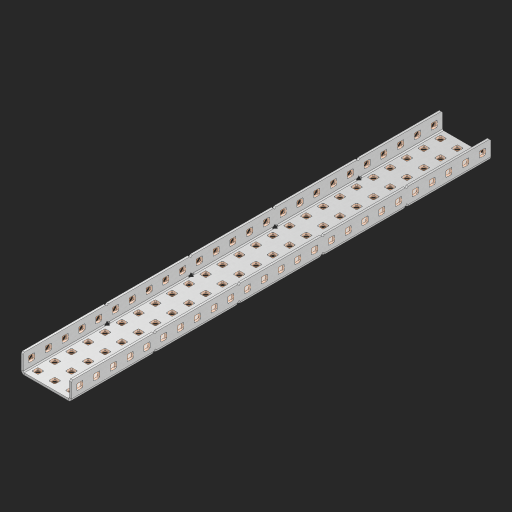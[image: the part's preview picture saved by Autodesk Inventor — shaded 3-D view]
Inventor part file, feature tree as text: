
AUTODESK INVENTOR PART (.ipt)
format: ipt  version: 2023 (Build 270158000, 158)  size: 1,567,232 bytes
history: native  units: in
note: dims shown in document units (in); Inventor stores cm internally (conversion verified against a paired STEP export)
features: other x130, extrude x124, sheet_metal_op x10, sketch x8, mirror x1, pattern_linear x1, chamfer x1
ambient origin geometry x8: Origin, YZ Plane, XZ Plane, XY Plane, X Axis, Y Axis, Z Axis, Center Point
bodies: Solid1 (feature_tree), Body (feature_tree)
feature tree (275):
  other  "Flange Pattern Plane"
  sheet_metal_op  "Flange Pattern"
  sheet_metal_op  "Body Pattern"
  other  "Arc Length"
  mirror  "Notch Mirror"
  pattern_linear  "Notch Pattern"  Spacing1=0.25in  [1 undecoded]
  chamfer  "End Chamfer"
  extrude  "Half Cut"  Depth=0.0625in
  sketch  "Sketch1"  dims[d0=1.5in]
  other  "Plate1"
  sketch  "Sketch2"  dims[d1=12.5in]
  other  "Plate2"
  sheet_metal_op  "Bend1"
  sheet_metal_op  "Corner1"
  sketch  "Sketch3"  dims[d2=0.0625in]
  other  "Flange Pattern Sketch"
  sketch  "Sketch7"  dims[d3=0.0625in]
  other  "Srf1"
  other  "Srf2"
  sketch  "Sketch8"  dims[d4=0.0312in]
  sketch  "Sketch9"  dims[d5=0.125in]
  other  "Srf91"
  sheet_metal_op  "Body Pattern Sketch"
  other  "Srf92"
  sketch  "Sketch13"  dims[d6=0.0625in]
  sketch  "Sketch14"  dims[d7=0.5in d8=90.0deg d9=0.0312in d10=0.25in d11=0.0625in d12=0.0625in d16=0.182in d17=0.02in d18=0.0625in d19=0.0in d20=0.25in d21=0.25in d46=0.172in d47=1.0in d48=0.0in d49=0.182in d50=0.02in d51=0.25in d52=0.25in d53=0.0625in d54=0.0in d55=0.172in d56=1.0in d57=0.0in d60=9.8425in d62=0.5in d63=1.1811in d65=0.5in d85=0.1473in d86=0.1782in d88=0.04in d89=0.0625in d90=0.0in d91=0.04in d92=0.0491in d95=2.5in d96=0.04in d97=0.25in d98=45.0deg d101=0.0in d102=2.497in d131=1.5in d132=9.8425in d134=0.5in d139=0.5in]
  other  "Srf856"
  other  "Srf1310"
  other  "Srf1311"
  other  "Srf1312"
  other  "Srf1376"
  other  "Srf1377"
  other  "Srf1728"
  other  "Srf1755"
  other  "Srf1878"
  other  "Srf1879"
  other  "Srf1880"
  other  "Srf1881"
  other  "Srf1882"
  other  "Srf1883"
  other  "Srf1884"
  other  "Srf1885"
  other  "Srf1886"
  other  "Srf1887"
  other  "Srf1888"
  other  "Srf1889"
  other  "Srf1890"
  other  "Srf1891"
  other  "Srf1892"
  other  "Srf1893"
  other  "Srf1894"
  other  "Srf1895"
  other  "Srf1896"
  other  "Srf1897"
  other  "Srf1898"
  other  "Srf1899"
  other  "Srf1900"
  other  "Srf1901"
  other  "Srf1902"
  other  "Srf1903"
  other  "Srf1904"
  other  "Srf1905"
  other  "Srf1906"
  other  "Srf1907"
  other  "Srf1908"
  other  "Srf1909"
  other  "Srf1910"
  other  "Srf1911"
  other  "Srf1912"
  other  "Srf1913"
  other  "Srf1914"
  other  "Srf1915"
  other  "Srf1916"
  other  "Srf1917"
  other  "Srf1918"
  other  "Srf1919"
  other  "Srf1920"
  other  "Srf1921"
  other  "Srf1942"
  other  "Srf1943"
  other  "Srf1944"
  other  "Srf1945"
  other  "Srf1946"
  other  "Srf1947"
  other  "Srf1948"
  other  "Srf1949"
  other  "Srf1950"
  other  "Srf1951"
  other  "Srf1952"
  other  "Srf1953"
  other  "Srf1954"
  other  "Srf1955"
  other  "Srf1956"
  other  "Srf1957"
  other  "Srf1958"
  other  "Srf1959"
  other  "Srf1960"
  other  "Srf1961"
  other  "Srf1962"
  other  "Srf1963"
  other  "Srf1964"
  other  "Srf1965"
  other  "Srf1966"
  other  "Srf1967"
  other  "Srf1968"
  other  "Srf1969"
  other  "Srf1970"
  other  "Srf1971"
  other  "Srf1972"
  other  "Srf1973"
  other  "Srf1974"
  other  "Srf1975"
  other  "Srf1976"
  other  "Srf1977"
  other  "Srf1978"
  other  "Srf1979"
  other  "Srf1980"
  other  "Srf1981"
  other  "Srf1982"
  other  "Srf1983"
  other  "Srf1984"
  other  "Srf1985"
  other  "Srf1986"
  other  "Srf1987"
  other  "Srf1988"
  other  "Srf1989"
  other  "Srf1990"
  other  "Srf1991"
  other  "Srf1992"
  other  "Srf1993"
  other  "Srf1994"
  other  "Srf1995"
  other  "Srf1996"
  other  "Srf1997"
  other  "Srf1998"
  other  "Srf1999"
  other  "Srf2000"
  other  "Srf2001"
  other  "Srf2002"
  other  "Srf2003"
  other  "Srf2004"
  other  "Srf2005"
  other  "Srf2006"
  other  "Srf2007"
  other  "Srf2008"
  other  "Srf2009"
  other  "Srf2010"
  sheet_metal_op  "Flange Stamp"
  sheet_metal_op  "Flange Circle"
  sheet_metal_op  "Body Stamp"
  sheet_metal_op  "Body Circle"
  sheet_metal_op  "Notch"
  extrude  "ExtrusionSrf2"  Depth=0.0625in
  extrude  "ExtrusionSrf92"  Depth=1.5in
  extrude  "ExtrusionSrf856"  Depth=0.02in
  extrude  "ExtrusionSrf1310"  Depth=0.0625in
  extrude  "ExtrusionSrf1311"  TaperAngle=0.0deg  [1 undecoded]
  extrude  "ExtrusionSrf1312"  Depth=0.25in
  extrude  "ExtrusionSrf1376"  Depth=0.25in
  extrude  "ExtrusionSrf1377"  Depth=1.5in
  extrude  "ExtrusionSrf1728"  Depth=1.5in TaperAngle=0.0deg
  extrude  "ExtrusionSrf1755"  Depth=1.5in
  extrude  "ExtrusionSrf1878"  Depth=0.02in
  extrude  "ExtrusionSrf1879"  Depth=0.25in
  extrude  "ExtrusionSrf1880"  Depth=0.25in
  extrude  "ExtrusionSrf1881"  Depth=0.0625in
  extrude  "ExtrusionSrf1882"  TaperAngle=0.0deg  [1 undecoded]
  extrude  "ExtrusionSrf1883"  Depth=1.5in
  extrude  "ExtrusionSrf1884"  Depth=1.5in TaperAngle=0.0deg
  extrude  "ExtrusionSrf1885"  Depth=1.5in
  extrude  "ExtrusionSrf1886"  Depth=1.5in
  extrude  "ExtrusionSrf1887"  Depth=1.5in
  extrude  "ExtrusionSrf1888"  Depth=1.5in
  extrude  "ExtrusionSrf1889"  Depth=1.5in
  extrude  "ExtrusionSrf1890"  Depth=0.0625in
  extrude  "ExtrusionSrf1891"  TaperAngle=0.0deg  [1 undecoded]
  extrude  "ExtrusionSrf1892"  Depth=1.5in
  extrude  "ExtrusionSrf1893"  Depth=1.5in
  extrude  "ExtrusionSrf1894"  Depth=1.5in
  extrude  "ExtrusionSrf1895"  Depth=0.25in TaperAngle=45.0deg
  extrude  "ExtrusionSrf1896"  TaperAngle=0.0deg  [1 undecoded]
  extrude  "ExtrusionSrf1897"  Depth=1.5in
  extrude  "ExtrusionSrf1898"  Depth=1.5in
  extrude  "ExtrusionSrf1899"  Depth=1.5in
  extrude  "ExtrusionSrf1900"  Depth=1.5in
  extrude  "ExtrusionSrf1901"  Depth=1.5in
  extrude  "ExtrusionSrf1902"  [1 undecoded]
  extrude  "ExtrusionSrf1903"  [1 undecoded]
  extrude  "ExtrusionSrf1904"  [1 undecoded]
  extrude  "ExtrusionSrf1905"  [1 undecoded]
  extrude  "ExtrusionSrf1906"  [1 undecoded]
  extrude  "ExtrusionSrf1907"  [1 undecoded]
  extrude  "ExtrusionSrf1908"  [1 undecoded]
  extrude  "ExtrusionSrf1909"  [1 undecoded]
  extrude  "ExtrusionSrf1910"  [1 undecoded]
  extrude  "ExtrusionSrf1911"  [1 undecoded]
  extrude  "ExtrusionSrf1912"  [1 undecoded]
  extrude  "ExtrusionSrf1913"  [1 undecoded]
  extrude  "ExtrusionSrf1914"  [1 undecoded]
  extrude  "ExtrusionSrf1915"  [1 undecoded]
  extrude  "ExtrusionSrf1916"  [1 undecoded]
  extrude  "ExtrusionSrf1917"  [1 undecoded]
  extrude  "ExtrusionSrf1918"  [1 undecoded]
  extrude  "ExtrusionSrf1919"  [1 undecoded]
  extrude  "ExtrusionSrf1920"  [1 undecoded]
  extrude  "ExtrusionSrf1921"  [1 undecoded]
  extrude  "ExtrusionSrf1942"  [1 undecoded]
  extrude  "ExtrusionSrf1943"  [1 undecoded]
  extrude  "ExtrusionSrf1944"  [1 undecoded]
  extrude  "ExtrusionSrf1945"  [1 undecoded]
  extrude  "ExtrusionSrf1946"  [1 undecoded]
  extrude  "ExtrusionSrf1947"  [1 undecoded]
  extrude  "ExtrusionSrf1948"  [1 undecoded]
  extrude  "ExtrusionSrf1949"  [1 undecoded]
  extrude  "ExtrusionSrf1950"  [1 undecoded]
  extrude  "ExtrusionSrf1951"  [1 undecoded]
  extrude  "ExtrusionSrf1952"  [1 undecoded]
  extrude  "ExtrusionSrf1953"  [1 undecoded]
  extrude  "ExtrusionSrf1954"  [1 undecoded]
  extrude  "ExtrusionSrf1955"  [1 undecoded]
  extrude  "ExtrusionSrf1956"  [1 undecoded]
  extrude  "ExtrusionSrf1957"  [1 undecoded]
  extrude  "ExtrusionSrf1958"  [1 undecoded]
  extrude  "ExtrusionSrf1959"  [1 undecoded]
  extrude  "ExtrusionSrf1960"  [1 undecoded]
  extrude  "ExtrusionSrf1961"  [1 undecoded]
  extrude  "ExtrusionSrf1962"  [1 undecoded]
  extrude  "ExtrusionSrf1963"  [1 undecoded]
  extrude  "ExtrusionSrf1964"  [1 undecoded]
  extrude  "ExtrusionSrf1965"  [1 undecoded]
  extrude  "ExtrusionSrf1966"  [1 undecoded]
  extrude  "ExtrusionSrf1967"  [1 undecoded]
  extrude  "ExtrusionSrf1968"  [1 undecoded]
  extrude  "ExtrusionSrf1969"  [1 undecoded]
  extrude  "ExtrusionSrf1970"  [1 undecoded]
  extrude  "ExtrusionSrf1971"  [1 undecoded]
  extrude  "ExtrusionSrf1972"  [1 undecoded]
  extrude  "ExtrusionSrf1973"  [1 undecoded]
  extrude  "ExtrusionSrf1974"  [1 undecoded]
  extrude  "ExtrusionSrf1975"  [1 undecoded]
  extrude  "ExtrusionSrf1976"  [1 undecoded]
  extrude  "ExtrusionSrf1977"  [1 undecoded]
  extrude  "ExtrusionSrf1978"  [1 undecoded]
  extrude  "ExtrusionSrf1979"  [1 undecoded]
  extrude  "ExtrusionSrf1980"  [1 undecoded]
  extrude  "ExtrusionSrf1981"  [1 undecoded]
  extrude  "ExtrusionSrf1982"  [1 undecoded]
  extrude  "ExtrusionSrf1983"  [1 undecoded]
  extrude  "ExtrusionSrf1984"  [1 undecoded]
  extrude  "ExtrusionSrf1985"  [1 undecoded]
  extrude  "ExtrusionSrf1986"  [1 undecoded]
  extrude  "ExtrusionSrf1987"  [1 undecoded]
  extrude  "ExtrusionSrf1988"  [1 undecoded]
  extrude  "ExtrusionSrf1989"  [1 undecoded]
  extrude  "ExtrusionSrf1990"  [1 undecoded]
  extrude  "ExtrusionSrf1991"  [1 undecoded]
  extrude  "ExtrusionSrf1992"  [1 undecoded]
  extrude  "ExtrusionSrf1993"  [1 undecoded]
  extrude  "ExtrusionSrf1994"  [1 undecoded]
  extrude  "ExtrusionSrf1995"  [1 undecoded]
  extrude  "ExtrusionSrf1996"  [1 undecoded]
  extrude  "ExtrusionSrf1997"  [1 undecoded]
  extrude  "ExtrusionSrf1998"  [1 undecoded]
  extrude  "ExtrusionSrf1999"  [1 undecoded]
  extrude  "ExtrusionSrf2000"  [1 undecoded]
  extrude  "ExtrusionSrf2001"  [1 undecoded]
  extrude  "ExtrusionSrf2002"  [1 undecoded]
  extrude  "ExtrusionSrf2003"  [1 undecoded]
  extrude  "ExtrusionSrf2004"  [1 undecoded]
  extrude  "ExtrusionSrf2005"  [1 undecoded]
  extrude  "ExtrusionSrf2006"  [1 undecoded]
  extrude  "ExtrusionSrf2007"  [1 undecoded]
  extrude  "ExtrusionSrf2008"  [1 undecoded]
  extrude  "ExtrusionSrf2009"  [1 undecoded]
  extrude  "ExtrusionSrf2010"  [1 undecoded]
note: 94 required parameter values undecoded (feature->parameter linkage not recoverable at this tier; creation-order binding heuristic only, values carry confidence <= 0.55)
